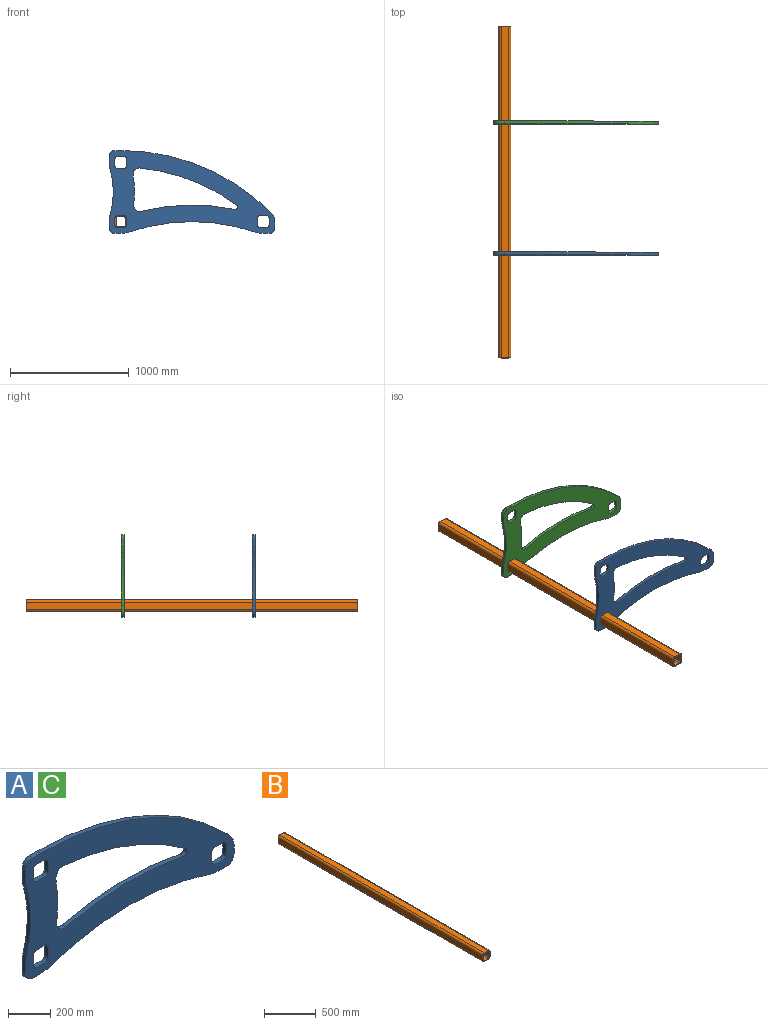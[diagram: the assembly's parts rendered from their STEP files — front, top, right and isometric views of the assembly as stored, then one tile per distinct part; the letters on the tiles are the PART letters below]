
ASSEMBLY  parts=3 mates=4
PART A: 49 faces, bbox 1400x25x700 mm
  f0: plane 50x25mm, normal (-1,0,0), area 1250mm2, adj f1,f46,f47,f48
  f1: cylinder r=200mm len=55.3mm, axis (0,1,0), area 1400.8mm2, adj f0,f2,f47,f48
  f2: cylinder r=704.15mm len=389.4mm, axis (0,1,0), area 9863.5mm2, adj f1,f3,f47,f48
  f3: cylinder r=200mm len=55.3mm, axis (0,1,0), area 1400.8mm2, adj f2,f4,f47,f48
  f4: plane 50x25mm, normal (-1,0,0), area 1250mm2, adj f3,f5,f47,f48
  f5: cylinder r=50mm len=50mm, axis (0,1,0), area 1963.5mm2, adj f4,f6,f47,f48
  f6: plane 50x25mm, normal (0,0,-1), area 1250mm2, adj f5,f7,f47,f48
  f7: cylinder r=200mm len=64.87mm, axis (0,1,0), area 1651.5mm2, adj f6,f8,f47,f48
  f8: cylinder r=1650mm len=1070.27mm, axis (0,1,0), area 27249.5mm2, adj f7,f9,f47,f48
  f9: cylinder r=200mm len=64.87mm, axis (0,1,0), area 1651.5mm2, adj f8,f10,f47,f48
  f10: plane 50x25mm, normal (0,0,-1), area 1250mm2, adj f9,f11,f47,f48
  f11: cylinder r=50mm len=50mm, axis (0,1,0), area 1963.5mm2, adj f10,f12,f47,f48
  f12: plane 50x25mm, normal (1,0,0), area 1250mm2, adj f11,f13,f47,f48
  f13: cylinder r=100mm len=70.41mm, axis (0,1,0), area 1953mm2, adj f12,f14,f47,f48
  f14: cylinder r=1790mm len=1271.01mm, axis (0,1,0), area 35333.8mm2, adj f13,f15,f47,f48
  f15: plane 50x25mm, normal (0,0,1), area 1250mm2, adj f14,f46,f47,f48
  f16: plane 60x25mm, normal (-1,0,0), area 1500mm2, adj f17,f42,f47,f48
  f17: cylinder r=20mm len=25mm, axis (0,1,0), area 785.4mm2, adj f16,f18,f47,f48
  f18: plane 60x25mm, normal (0,0,1), area 1500mm2, adj f17,f19,f47,f48
  f19: cylinder r=20mm len=25mm, axis (0,1,0), area 785.4mm2, adj f18,f20,f47,f48
  f20: plane 60x25mm, normal (1,0,0), area 1500mm2, adj f19,f21,f47,f48
  f21: cylinder r=20mm len=25mm, axis (0,1,0), area 785.4mm2, adj f20,f22,f47,f48
  f22: plane 60x25mm, normal (0,0,-1), area 1500mm2, adj f21,f42,f47,f48
  f23: plane 60x25mm, normal (-1,0,0), area 1500mm2, adj f24,f43,f47,f48
  f24: cylinder r=20mm len=25mm, axis (0,1,0), area 785.4mm2, adj f23,f25,f47,f48
  f25: plane 60x25mm, normal (0,0,1), area 1500mm2, adj f24,f26,f47,f48
  f26: cylinder r=20mm len=25mm, axis (0,1,0), area 785.4mm2, adj f25,f27,f47,f48
  f27: plane 60x25mm, normal (1,0,0), area 1500mm2, adj f26,f28,f47,f48
  f28: cylinder r=20mm len=25mm, axis (0,1,0), area 785.4mm2, adj f27,f29,f47,f48
  f29: plane 60x25mm, normal (0,0,-1), area 1500mm2, adj f28,f43,f47,f48
  f30: cylinder r=20mm len=25mm, axis (0,1,0), area 785.4mm2, adj f31,f44,f47,f48
  f31: plane 60x25mm, normal (0,0,-1), area 1500mm2, adj f30,f32,f47,f48
  f32: cylinder r=20mm len=25mm, axis (0,1,0), area 785.4mm2, adj f31,f33,f47,f48
  f33: plane 60x25mm, normal (-1,0,0), area 1500mm2, adj f32,f34,f47,f48
  f34: cylinder r=20mm len=25mm, axis (0,1,0), area 785.4mm2, adj f33,f35,f47,f48
  f35: plane 60x25mm, normal (0,0,1), area 1500mm2, adj f34,f36,f47,f48
  f36: cylinder r=20mm len=25mm, axis (0,1,0), area 785.4mm2, adj f35,f44,f47,f48
  f37: cylinder r=50mm len=62mm, axis (0,1,0), area 2419.2mm2, adj f38,f45,f47,f48
  f38: cylinder r=884.15mm len=252.24mm, axis (0,1,0), area 6328.9mm2, adj f37,f39,f47,f48
  f39: cylinder r=50mm len=58.17mm, axis (0,1,0), area 2288.2mm2, adj f38,f40,f47,f48
  f40: cylinder r=1650mm len=820.98mm, axis (0,1,0), area 22241.8mm2, adj f39,f41,f47,f48
  f41: cylinder r=20mm len=36.1mm, axis (0,1,0), area 1355.4mm2, adj f40,f45,f47,f48
  f42: cylinder r=20mm len=25mm, axis (0,1,0), area 785.4mm2, adj f16,f22,f47,f48
  f43: cylinder r=20mm len=25mm, axis (0,1,0), area 785.4mm2, adj f23,f29,f47,f48
  f44: plane 60x25mm, normal (1,0,0), area 1500mm2, adj f30,f36,f47,f48
  f45: cylinder r=1790mm len=792.23mm, axis (0,1,0), area 19974.8mm2, adj f37,f41,f47,f48
  f46: cylinder r=50mm len=50mm, axis (0,1,0), area 1963.5mm2, adj f0,f15,f47,f48
  f47: plane 1400x700mm, normal (0,-1,0), area 445349.2mm2, adj f0,f1,f2,f3,f4,f5,f6,f7
  f48: plane 1400x700mm, normal (0,1,0), area 445349.2mm2, adj f0,f1,f2,f3,f4,f5,f6,f7
PART B: 18 faces, bbox 100x2800x100 mm
  f0: plane 2800x60mm, normal (1,0,0), area 168000mm2, adj f1,f15,f16,f17
  f1: cylinder r=20mm len=2800mm, axis (0,1,0), area 87964.6mm2, adj f0,f2,f16,f17
  f2: plane 2800x60mm, normal (0,0,1), area 168000mm2, adj f1,f3,f16,f17
  f3: cylinder r=20mm len=2800mm, axis (0,1,0), area 87964.6mm2, adj f2,f4,f16,f17
  f4: plane 2800x60mm, normal (-1,0,0), area 168000mm2, adj f3,f5,f16,f17
  f5: cylinder r=20mm len=2800mm, axis (0,1,0), area 87964.6mm2, adj f4,f6,f16,f17
  f6: plane 2800x60mm, normal (0,0,-1), area 168000mm2, adj f5,f15,f16,f17
  f7: cylinder r=10mm len=2800mm, axis (0,1,0), area 43982.3mm2, adj f8,f14,f16,f17
  f8: plane 2800x60mm, normal (0,0,-1), area 168000mm2, adj f7,f9,f16,f17
  f9: cylinder r=10mm len=2800mm, axis (0,1,0), area 43982.3mm2, adj f8,f10,f16,f17
  f10: plane 2800x60mm, normal (-1,0,0), area 168000mm2, adj f9,f11,f16,f17
  f11: cylinder r=10mm len=2800mm, axis (0,1,0), area 43982.3mm2, adj f10,f12,f16,f17
  f12: plane 2800x60mm, normal (0,0,1), area 168000mm2, adj f11,f13,f16,f17
  f13: cylinder r=10mm len=2800mm, axis (0,1,0), area 43982.3mm2, adj f12,f14,f16,f17
  f14: plane 2800x60mm, normal (1,0,0), area 168000mm2, adj f7,f13,f16,f17
  f15: cylinder r=20mm len=2800mm, axis (0,1,0), area 87964.6mm2, adj f0,f6,f16,f17
  f16: plane 100x100mm, normal (0,-1,0), area 3342.5mm2, adj f0,f1,f2,f3,f4,f5,f6,f7
  f17: plane 100x100mm, normal (0,1,0), area 3342.5mm2, adj f0,f1,f2,f3,f4,f5,f6,f7
PART C: same geometry as A
PLACE A t=(-192.75,420.52,628.46)mm
PLACE B t=(-142.75,2327.32,678.46)mm
PLACE C t=(-192.75,1525.4,628.46)mm
MATE planar C.f6 <-> A.f6  axis (0,0,-1) through (-167.75,1512.9,578.46)mm
MATE planar A.f33 <-> B.f0  axis (-1,0,0) through (-92.75,408.02,678.46)mm
MATE planar C.f4 <-> A.f4  axis (-1,0,0) through (-242.75,1512.9,653.46)mm
MATE planar B.f6 <-> A.f35  axis (0,0,-1) through (-142.75,927.32,628.46)mm
